# Revit family: DTI_A3-AC-Panel-D6p-Frame-F
name_source: partatom
category: Doors
revit_build: Autodesk Revit 2016 (Build: 20150220_1215(x64)
units: mm (PartAtom-declared; Revit-internal decimal feet)

## family parameters
Always vertical = Yes
Cut with Voids When Loaded = No
Host = Wall
Room Calculation Point = No
Shared = No

## types (1)
- Panel D6P - Frame F
    Assembly Code = B2030230
    Frame Depth = 68 mm
    Frame Material = Meranti Wood
    Frame Thickness = 102 mm  [stored 0.334646 ft]
    Frame Type = Frame F
    Function = Interior
    Glass Mateial = Glass
    Height = 2100 mm
    Manufacturer = AC Doors
    Manufacturer Code = D6P - F
    Model = Glass Door
    Panel Height = 2032 mm
    Panel Material = Meranti Wood
    Panel Thickness = 44 mm  [stored 0.144357 ft]
    Panel Type = D6P
    Panel Width = 762 mm  [stored 2.5 ft]
    URL = www.acdoors.co.za
    Wall Closure = By host
    Width = 898 mm  [stored 2.94619 ft]

note: [stored X ft] marks values corroborated as IEEE doubles in the binary element streams (Revit-internal decimal feet)

## geometry (parser evidence)
native form markers: Sweep x7
no freeform markers — native parametric forms only
